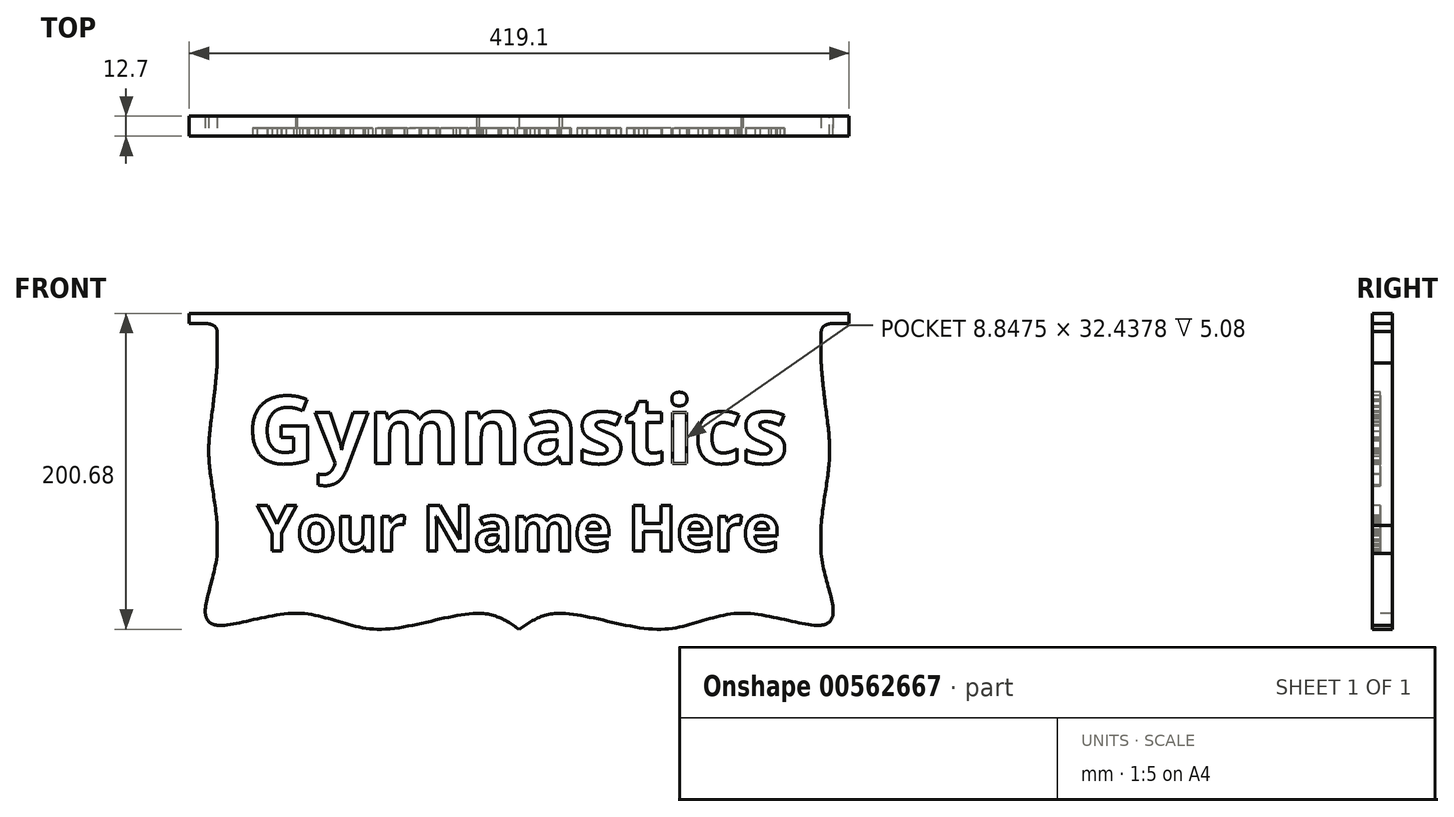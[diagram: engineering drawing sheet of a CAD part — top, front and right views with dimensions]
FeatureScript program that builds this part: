
annotation { "Feature Type Name" : "Feature", "Feature Type Description" : "" }
export const myFeature = defineFeature(function(context is Context, id is Id, definition is map)
    precondition{}
    {
        {
            var Q0;
            Q0=qCreatedBy(makeId("Front.planeOp"),FACE);
            var sketch = newSketch(context, id + "F0", { "sketchPlane" : qUnion([Q0])});
            skLineSegment(sketch, "E0.bottom", {"start": v(-209.55, 95.25) * mm, "end": v(209.55, 95.25) * mm});
            skLineSegment(sketch, "E0.top", {"start": v(-209.55, -95.25) * mm, "end": v(209.55, -95.25) * mm});
            skLineSegment(sketch, "E0.left", {"start": v(-209.55, 95.25) * mm, "end": v(-209.55, -95.25) * mm});
            skLineSegment(sketch, "E0.right", {"start": v(209.55, 95.25) * mm, "end": v(209.55, -95.25) * mm});
            skPoint(sketch, "E0.middle", {"position": v(0, 0) * mm});
            skSolve(sketch);
        }
        {
            var Q0;
            Q0=makeQuery(id+"F0.imprint","IMPRINT",FACE,{"disambiguationData":[TD([[makeQuery(id+"F0.imprint","IMPRINT",EDGE,{"derivedFrom":sQuery(id+"F0.wireOp",EDGE,"E0.bottom")}),-1.0]])]});
            extrude(context, id + "F1", {"entities" : qUnion([Q0]), "depth" : 12.7 * mm});
        }
        {
            var Q0;
            Q0=makeQuery(id+"F1.opExtrude","CAP_FACE",FACE,{"disambiguationData":[OSD([sQuery(id+"F0.wireOp",EDGE,"E0.bottom"),sQuery(id+"F0.wireOp",EDGE,"E0.top"),sQuery(id+"F0.wireOp",EDGE,"E0.left"),sQuery(id+"F0.wireOp",EDGE,"E0.right")])],"isStart":false});
            var sketch = newSketch(context, id + "F2", { "sketchPlane" : qUnion([Q0])});
            skText(sketch, "E1", { "text": "Gymnastics", "fontName": "OpenSans-Bold.ttf"});
            skText(sketch, "E2", { "text": "Your Name Here", "fontName": "OpenSans-Bold.ttf"});
            const initialGuessF2  = {"E1": [-0.17278, 0, 1, 0, 0.04278], "E2": [-0.16647, -0.05555, 1, 0, 0.02893]};
            skSetInitialGuess(sketch, initialGuessF2);
            skSolve(sketch);
        }
        {
            var Q0;
            Q0=qSketchRegion(id+"F2",true);
            extrude(context, id + "F3", {"entities" : qUnion([Q0]), "operationType" : NewBodyOperationType.REMOVE, "oppositeDirection" : true, "depth" : 5.08 * mm});
        }
        {
            var Q0;
            {var subQ0=sQuery(id+"F0.wireOp",EDGE,"E0.left");var subQ1=sQuery(id+"F0.wireOp",EDGE,"E0.bottom");var subQ2=sQuery(id+"F0.wireOp",EDGE,"E0.right");var subQ3=sQuery(id+"F0.wireOp",EDGE,"E0.top");Q0=makeQuery(id+"F3.boolean.opBoolean","SPLIT",FACE,{"disambiguationData":[TD([makeQuery(id+"F1.opExtrude","SWEPT_FACE",FACE,{"disambiguationData":[OSD([subQ1])]})])],"derivedFrom":makeQuery(id+"F1.opExtrude","CAP_FACE",FACE,{"disambiguationData":[OSD([subQ1,subQ3,subQ0,subQ2])],"isStart":false})});}
            var sketch = newSketch(context, id + "F4", { "sketchPlane" : qUnion([Q0])});
            skPoint(sketch, "E3", {"position": v(-191.77, 95.25) * mm});
            skPoint(sketch, "E4", {"position": v(-191.77, -95.25) * mm});
            skPoint(sketch, "E5", {"position": v(191.77, 95.25) * mm});
            skPoint(sketch, "E6", {"position": v(209.55, 88.9) * mm});
            skPoint(sketch, "E7", {"position": v(191.77, -95.25) * mm});
            skPoint(sketch, "E8", {"position": v(-209.55, 88.9) * mm});
            skLineSegment(sketch, "E9", {"start": v(-191.77, 95.25) * mm, "end": v(-191.77, -95.25) * mm});
            skLineSegment(sketch, "E10", {"start": v(-209.55, 88.9) * mm, "end": v(-191.77, 88.9) * mm});
            skLineSegment(sketch, "E11", {"start": v(191.77, -95.25) * mm, "end": v(191.77, 95.25) * mm});
            skLineSegment(sketch, "E12", {"start": v(209.55, 88.9) * mm, "end": v(191.77, 88.9) * mm});
            skPoint(sketch, "E13", {"position": v(-32.37, -40.44) * mm});
            skPoint(sketch, "E14", {"position": v(-37.84, -40.44) * mm});
            skSolve(sketch);
        }
        {
            var Q0;
            {var subQ3=sQuery(id+"F4.wireOp",EDGE,"E10");Q0=makeQuery(id+"F4.imprint","IMPRINT",FACE,{"disambiguationData":[TD([[makeQuery(id+"F4.imprint","IMPRINT",EDGE,{"derivedFrom":subQ3}),-1.0]])]});}
            var Q1;
            {var subQ3=sQuery(id+"F4.wireOp",EDGE,"E12");Q1=makeQuery(id+"F4.imprint","IMPRINT",FACE,{"disambiguationData":[TD([[makeQuery(id+"F4.imprint","IMPRINT",EDGE,{"derivedFrom":subQ3}),1.0]])]});}
            extrude(context, id + "F5", {"entities" : qUnion([Q0, Q1]), "operationType" : NewBodyOperationType.REMOVE, "oppositeDirection" : true, "depth" : 12.7 * mm});
        }
        {
            var Q0;
            {var subQ0=sQuery(id+"F0.wireOp",EDGE,"E0.left");var subQ1=sQuery(id+"F0.wireOp",EDGE,"E0.bottom");var subQ2=sQuery(id+"F0.wireOp",EDGE,"E0.right");var subQ3=sQuery(id+"F0.wireOp",EDGE,"E0.top");Q0=makeQuery(id+"F3.boolean.opBoolean","SPLIT",FACE,{"disambiguationData":[TD([makeQuery(id+"F1.opExtrude","SWEPT_FACE",FACE,{"disambiguationData":[OSD([subQ1])]})])],"derivedFrom":makeQuery(id+"F1.opExtrude","CAP_FACE",FACE,{"disambiguationData":[OSD([subQ1,subQ3,subQ0,subQ2])],"isStart":false})});}
            var sketch = newSketch(context, id + "F6", { "sketchPlane" : qUnion([Q0])});
            skPoint(sketch, "E15", {"position": v(-191.77, 38.1) * mm});
            skPoint(sketch, "E16", {"position": v(-191.77, 0) * mm});
            skPoint(sketch, "E17", {"position": v(-191.77, -57.15) * mm});
            skPoint(sketch, "E18", {"position": v(-140.97, -95.25) * mm});
            skPoint(sketch, "E19", {"position": v(-90.17, -95.25) * mm});
            skPoint(sketch, "E20", {"position": v(0, -95.25) * mm});
            skPoint(sketch, "E21", {"position": v(90.17, -95.25) * mm});
            skPoint(sketch, "E22", {"position": v(140.97, -95.25) * mm});
            skPoint(sketch, "E23", {"position": v(191.77, -57.15) * mm});
            skPoint(sketch, "E24", {"position": v(191.77, 0) * mm});
            skPoint(sketch, "E25", {"position": v(191.77, 38.1) * mm});
            skLineSegment(sketch, "E26", {"start": v(-191.77, 0) * mm, "end": v(-196.85, 0) * mm});
            skLineSegment(sketch, "E27", {"start": v(-191.77, 38.1) * mm, "end": v(-194.3, 38.1) * mm});
            skLineSegment(sketch, "E28", {"start": v(-191.77, -95.25) * mm, "end": v(-199.39, -95.25) * mm});
            skLineSegment(sketch, "E29", {"start": v(-191.77, -95.25) * mm, "end": v(-191.77, -102.87) * mm});
            skLineSegment(sketch, "E30", {"start": v(-90.17, -95.25) * mm, "end": v(-90.17, -105.41) * mm});
            skLineSegment(sketch, "E31", {"start": v(191.77, 38.1) * mm, "end": v(194.31, 38.1) * mm});
            skLineSegment(sketch, "E32", {"start": v(191.77, 0) * mm, "end": v(196.85, 0) * mm});
            skLineSegment(sketch, "E33", {"start": v(191.77, -95.25) * mm, "end": v(199.4, -95.25) * mm});
            skLineSegment(sketch, "E34", {"start": v(191.77, -95.25) * mm, "end": v(191.77, -102.87) * mm});
            skLineSegment(sketch, "E35", {"start": v(90.17, -95.25) * mm, "end": v(90.17, -105.41) * mm});
            skPoint(sketch, "E36", {"position": v(25.4, -95.25) * mm});
            skPoint(sketch, "E37", {"position": v(-25.4, -95.25) * mm});
            skLineSegment(sketch, "E38", {"start": v(0, -95.25) * mm, "end": v(0, -105.41) * mm});
            skPoint(sketch, "E39", {"position": v(199.4, 88.9) * mm});
            skPoint(sketch, "E40", {"position": v(191.77, 83.82) * mm});
            skPoint(sketch, "E41", {"position": v(194.31, 88.9) * mm});
            skLineSegment(sketch, "E42", {"start": v(194.31, 88.9) * mm, "end": v(194.31, 87.63) * mm});
            skFitSpline(sketch, "E43", {"points": [v(0, -105.41) * mm, v(25.4, -95.25) * mm, v(90.17, -105.41) * mm, v(140.97, -95.25) * mm, v(191.77, -102.87) * mm, v(199.4, -95.25) * mm, v(191.77, -57.15) * mm, v(196.85, 0) * mm, v(194.31, 38.1) * mm, v(191.77, 83.82) * mm, v(194.31, 87.63) * mm, v(199.4, 88.9) * mm], "startDerivative": vector(254.46, 176.78) * mm, "endDerivative": vector(162.96, 9.49) * mm});
            skPoint(sketch, "E44", {"position": v(-199.39, 88.9) * mm});
            skPoint(sketch, "E45", {"position": v(-191.77, 83.82) * mm});
            skPoint(sketch, "E46", {"position": v(-194.3, 88.9) * mm});
            skLineSegment(sketch, "E47", {"start": v(-194.3, 88.9) * mm, "end": v(-194.3, 87.63) * mm});
            skFitSpline(sketch, "E48", {"points": [v(0, -105.41) * mm, v(-25.4, -95.25) * mm, v(-90.17, -105.41) * mm, v(-140.97, -95.25) * mm, v(-191.77, -102.87) * mm, v(-199.39, -95.25) * mm, v(-191.77, -57.15) * mm, v(-196.85, 0) * mm, v(-194.3, 38.1) * mm, v(-191.77, 83.82) * mm, v(-194.3, 87.63) * mm, v(-199.39, 88.9) * mm], "startDerivative": vector(-252.39, 175.34) * mm, "endDerivative": vector(-141.61, 8.53) * mm});
            skSolve(sketch);
        }
        {
            var Q0;
            Q0=qSketchRegion(id+"F6",true);
            var Q1;
            {var subQ0=sQuery(id+"F6.wireOp",EDGE,"9e0a6239-fdb5-4647-a296-c43551efd45f");var subQ1=makeQuery(id+"F5.boolean.opBoolean","COPY",EDGE,{"derivedFrom":makeQuery(id+"F5.opExtrude","CAP_EDGE",EDGE,{"disambiguationData":[OSD([sQuery(id+"F4.wireOp",EDGE,"E11")])],"isStart":true})});var subQ2=makeQuery(id+"F6.imprint","INTERSECT",VERTEX,{"disambiguationData":[OD(0.0)],"derivedFrom":[subQ1,subQ0]});Q1=makeQuery(id+"F6.imprint","IMPRINT",FACE,{"disambiguationData":[TD([[makeQuery(id+"F6.imprint","IMPRINT",EDGE,{"disambiguationData":[TD([[subQ2,-1.0]])],"derivedFrom":subQ0}),1.0]])]});}
            var Q2;
            {var subQ0=sQuery(id+"F6.wireOp",EDGE,"d2f81a62-16b6-484c-80cf-df5878542265");var subQ1=makeQuery(id+"F5.boolean.opBoolean","COPY",EDGE,{"derivedFrom":makeQuery(id+"F5.opExtrude","CAP_EDGE",EDGE,{"disambiguationData":[OSD([sQuery(id+"F4.wireOp",EDGE,"E9")])],"isStart":true})});var subQ2=makeQuery(id+"F6.imprint","INTERSECT",VERTEX,{"disambiguationData":[OD(0.0)],"derivedFrom":[subQ1,subQ0]});Q2=makeQuery(id+"F6.imprint","IMPRINT",FACE,{"disambiguationData":[TD([[makeQuery(id+"F6.imprint","IMPRINT",EDGE,{"disambiguationData":[TD([[subQ2,-1.0]])],"derivedFrom":subQ0}),-1.0]])]});}
            var Q3;
            {var subQ0=sQuery(id+"F6.wireOp",EDGE,"E43");var subQ1=makeQuery(id+"F5.boolean.opBoolean","COPY",EDGE,{"derivedFrom":makeQuery(id+"F5.opExtrude","CAP_EDGE",EDGE,{"disambiguationData":[OSD([sQuery(id+"F4.wireOp",EDGE,"E11")])],"isStart":true})});var subQ2=makeQuery(id+"F6.imprint","INTERSECT",VERTEX,{"disambiguationData":[OD(2.0)],"derivedFrom":[subQ1,subQ0]});Q3=makeQuery(id+"F6.imprint","IMPRINT",FACE,{"disambiguationData":[TD([[makeQuery(id+"F6.imprint","IMPRINT",EDGE,{"disambiguationData":[TD([[subQ2,-1.0]])],"derivedFrom":subQ0}),-1.0]])]});}
            var Q4;
            {var subQ0=sQuery(id+"F6.wireOp",EDGE,"E48");var subQ1=makeQuery(id+"F5.boolean.opBoolean","COPY",EDGE,{"derivedFrom":makeQuery(id+"F5.opExtrude","CAP_EDGE",EDGE,{"disambiguationData":[OSD([sQuery(id+"F4.wireOp",EDGE,"E9")])],"isStart":true})});var subQ2=makeQuery(id+"F6.imprint","INTERSECT",VERTEX,{"disambiguationData":[OD(2.0)],"derivedFrom":[subQ1,subQ0]});Q4=makeQuery(id+"F6.imprint","IMPRINT",FACE,{"disambiguationData":[TD([[makeQuery(id+"F6.imprint","IMPRINT",EDGE,{"disambiguationData":[TD([[subQ2,-1.0]])],"derivedFrom":subQ0}),1.0]])]});}
            var Q5;
            {var subQ0=sQuery(id+"F6.wireOp",EDGE,"E48");var subQ1=makeQuery(id+"F5.boolean.opBoolean","COPY",EDGE,{"derivedFrom":makeQuery(id+"F5.opExtrude","CAP_EDGE",EDGE,{"disambiguationData":[OSD([sQuery(id+"F4.wireOp",EDGE,"E9")])],"isStart":true})});var subQ2=makeQuery(id+"F6.imprint","INTERSECT",VERTEX,{"disambiguationData":[OD(0.0)],"derivedFrom":[subQ1,subQ0]});Q5=makeQuery(id+"F6.imprint","IMPRINT",FACE,{"disambiguationData":[TD([[makeQuery(id+"F6.imprint","IMPRINT",EDGE,{"disambiguationData":[TD([[subQ2,-1.0]])],"derivedFrom":subQ0}),1.0]])]});}
            var Q6;
            {var subQ0=sQuery(id+"F6.wireOp",EDGE,"E43");var subQ1=makeQuery(id+"F5.boolean.opBoolean","COPY",EDGE,{"derivedFrom":makeQuery(id+"F5.opExtrude","CAP_EDGE",EDGE,{"disambiguationData":[OSD([sQuery(id+"F4.wireOp",EDGE,"E11")])],"isStart":true})});var subQ2=makeQuery(id+"F6.imprint","INTERSECT",VERTEX,{"disambiguationData":[OD(0.0)],"derivedFrom":[subQ1,subQ0]});Q6=makeQuery(id+"F6.imprint","IMPRINT",FACE,{"disambiguationData":[TD([[makeQuery(id+"F6.imprint","IMPRINT",EDGE,{"disambiguationData":[TD([[subQ2,-1.0]])],"derivedFrom":subQ0}),-1.0]])]});}
            extrude(context, id + "F7", {"entities" : qUnion([Q0, Q1, Q2, Q3, Q4, Q5, Q6]), "operationType" : NewBodyOperationType.REMOVE, "oppositeDirection" : true, "depth" : 12.7 * mm, "offsetDistance" : 25.4 * mm});
        }
        {
            var Q0;
            {var subQ0=sQuery(id+"F6.wireOp",EDGE,"E26");Q0=makeQuery(id+"F6.imprint","IMPRINT",FACE,{"disambiguationData":[TD([[makeQuery(id+"F6.imprint","IMPRINT",EDGE,{"derivedFrom":subQ0}),-1.0]])]});}
            var Q1;
            {var subQ0=sQuery(id+"F6.wireOp",EDGE,"E26");Q1=makeQuery(id+"F6.imprint","IMPRINT",FACE,{"disambiguationData":[TD([[makeQuery(id+"F6.imprint","IMPRINT",EDGE,{"derivedFrom":subQ0}),1.0]])]});}
            var Q2;
            {var subQ0=sQuery(id+"F6.wireOp",EDGE,"E27");Q2=makeQuery(id+"F6.imprint","IMPRINT",FACE,{"disambiguationData":[TD([[makeQuery(id+"F6.imprint","IMPRINT",EDGE,{"derivedFrom":subQ0}),-1.0]])]});}
            var Q3;
            {var subQ0=sQuery(id+"F6.wireOp",EDGE,"E28");Q3=makeQuery(id+"F6.imprint","IMPRINT",FACE,{"disambiguationData":[TD([[makeQuery(id+"F6.imprint","IMPRINT",EDGE,{"derivedFrom":subQ0}),-1.0]])]});}
            var Q4;
            {var subQ0=sQuery(id+"F6.wireOp",EDGE,"E28");Q4=makeQuery(id+"F6.imprint","IMPRINT",FACE,{"disambiguationData":[TD([[makeQuery(id+"F6.imprint","IMPRINT",EDGE,{"derivedFrom":subQ0}),1.0]])]});}
            var Q5;
            {var subQ0=sQuery(id+"F6.wireOp",EDGE,"E29");Q5=makeQuery(id+"F6.imprint","IMPRINT",FACE,{"disambiguationData":[TD([[makeQuery(id+"F6.imprint","IMPRINT",EDGE,{"derivedFrom":subQ0}),1.0]])]});}
            var Q6;
            {var subQ0=sQuery(id+"F6.wireOp",EDGE,"E30");Q6=makeQuery(id+"F6.imprint","IMPRINT",FACE,{"disambiguationData":[TD([[makeQuery(id+"F6.imprint","IMPRINT",EDGE,{"derivedFrom":subQ0}),-1.0]])]});}
            var Q7;
            {var subQ0=sQuery(id+"F6.wireOp",EDGE,"E30");Q7=makeQuery(id+"F6.imprint","IMPRINT",FACE,{"disambiguationData":[TD([[makeQuery(id+"F6.imprint","IMPRINT",EDGE,{"derivedFrom":subQ0}),1.0]])]});}
            var Q8;
            {var subQ0=sQuery(id+"F6.wireOp",EDGE,"E38");Q8=makeQuery(id+"F6.imprint","IMPRINT",FACE,{"disambiguationData":[TD([[makeQuery(id+"F6.imprint","IMPRINT",EDGE,{"derivedFrom":subQ0}),-1.0]])]});}
            var Q9;
            {var subQ0=sQuery(id+"F6.wireOp",EDGE,"E38");Q9=makeQuery(id+"F6.imprint","IMPRINT",FACE,{"disambiguationData":[TD([[makeQuery(id+"F6.imprint","IMPRINT",EDGE,{"derivedFrom":subQ0}),1.0]])]});}
            var Q10;
            {var subQ0=sQuery(id+"F6.wireOp",EDGE,"9e0a6239-fdb5-4647-a296-c43551efd45f");var subQ1=sQuery(id+"F6.wireOp",EDGE,"E35");var subQ2=makeQuery(id+"F6.imprint","INTERSECT",VERTEX,{"derivedFrom":[subQ1,subQ0]});Q10=makeQuery(id+"F6.imprint","IMPRINT",FACE,{"disambiguationData":[TD([[makeQuery(id+"F6.imprint","IMPRINT",EDGE,{"disambiguationData":[TD([[subQ2,1.0]])],"derivedFrom":subQ1}),-1.0]])]});}
            var Q11;
            {var subQ0=sQuery(id+"F6.wireOp",EDGE,"9e0a6239-fdb5-4647-a296-c43551efd45f");var subQ1=sQuery(id+"F6.wireOp",EDGE,"E35");var subQ2=makeQuery(id+"F6.imprint","INTERSECT",VERTEX,{"derivedFrom":[subQ1,subQ0]});Q11=makeQuery(id+"F6.imprint","IMPRINT",FACE,{"disambiguationData":[TD([[makeQuery(id+"F6.imprint","IMPRINT",EDGE,{"disambiguationData":[TD([[subQ2,1.0]])],"derivedFrom":subQ1}),1.0]])]});}
            var Q12;
            {var subQ0=sQuery(id+"F6.wireOp",EDGE,"E34");Q12=makeQuery(id+"F6.imprint","IMPRINT",FACE,{"disambiguationData":[TD([[makeQuery(id+"F6.imprint","IMPRINT",EDGE,{"derivedFrom":subQ0}),-1.0]])]});}
            var Q13;
            {var subQ0=sQuery(id+"F6.wireOp",EDGE,"E33");Q13=makeQuery(id+"F6.imprint","IMPRINT",FACE,{"disambiguationData":[TD([[makeQuery(id+"F6.imprint","IMPRINT",EDGE,{"derivedFrom":subQ0}),-1.0]])]});}
            var Q14;
            {var subQ0=sQuery(id+"F6.wireOp",EDGE,"E33");Q14=makeQuery(id+"F6.imprint","IMPRINT",FACE,{"disambiguationData":[TD([[makeQuery(id+"F6.imprint","IMPRINT",EDGE,{"derivedFrom":subQ0}),1.0]])]});}
            var Q15;
            {var subQ0=sQuery(id+"F6.wireOp",EDGE,"E32");Q15=makeQuery(id+"F6.imprint","IMPRINT",FACE,{"disambiguationData":[TD([[makeQuery(id+"F6.imprint","IMPRINT",EDGE,{"derivedFrom":subQ0}),-1.0]])]});}
            var Q16;
            {var subQ0=sQuery(id+"F6.wireOp",EDGE,"E31");Q16=makeQuery(id+"F6.imprint","IMPRINT",FACE,{"disambiguationData":[TD([[makeQuery(id+"F6.imprint","IMPRINT",EDGE,{"derivedFrom":subQ0}),-1.0]])]});}
            var Q17;
            {var subQ0=sQuery(id+"F6.wireOp",EDGE,"E31");Q17=makeQuery(id+"F6.imprint","IMPRINT",FACE,{"disambiguationData":[TD([[makeQuery(id+"F6.imprint","IMPRINT",EDGE,{"derivedFrom":subQ0}),1.0]])]});}
            var Q18;
            {var subQ0=sQuery(id+"F6.wireOp",EDGE,"9e0a6239-fdb5-4647-a296-c43551efd45f");var subQ1=makeQuery(id+"F6.imprint","IMPRINT",VERTEX,{"derivedFrom":subQ0});Q18=makeQuery(id+"F6.imprint","IMPRINT",FACE,{"disambiguationData":[TD([[makeQuery(id+"F6.imprint","IMPRINT",EDGE,{"disambiguationData":[TD([[subQ1,1.0]])],"derivedFrom":subQ0}),-1.0]])]});}
            var Q19;
            {var subQ0=sQuery(id+"F6.wireOp",EDGE,"E42");Q19=makeQuery(id+"F6.imprint","IMPRINT",FACE,{"disambiguationData":[TD([[makeQuery(id+"F6.imprint","IMPRINT",EDGE,{"derivedFrom":subQ0}),-1.0]])]});}
            var Q20;
            {var subQ0=sQuery(id+"F6.wireOp",EDGE,"E42");Q20=makeQuery(id+"F6.imprint","IMPRINT",FACE,{"disambiguationData":[TD([[makeQuery(id+"F6.imprint","IMPRINT",EDGE,{"derivedFrom":subQ0}),1.0]])]});}
            var Q21;
            {var subQ0=sQuery(id+"F6.wireOp",EDGE,"E47");Q21=makeQuery(id+"F6.imprint","IMPRINT",FACE,{"disambiguationData":[TD([[makeQuery(id+"F6.imprint","IMPRINT",EDGE,{"derivedFrom":subQ0}),1.0]])]});}
            var Q22;
            {var subQ0=sQuery(id+"F6.wireOp",EDGE,"E47");Q22=makeQuery(id+"F6.imprint","IMPRINT",FACE,{"disambiguationData":[TD([[makeQuery(id+"F6.imprint","IMPRINT",EDGE,{"derivedFrom":subQ0}),-1.0]])]});}
            extrude(context, id + "F8", {"entities" : qUnion([Q0, Q1, Q2, Q3, Q4, Q5, Q6, Q7, Q8, Q9, Q10, Q11, Q12, Q13, Q14, Q15, Q16, Q17, Q18, Q19, Q20, Q21, Q22]), "operationType" : NewBodyOperationType.ADD, "depth" : -12.7 * mm, "offsetDistance" : 25.4 * mm});
        }
    });
